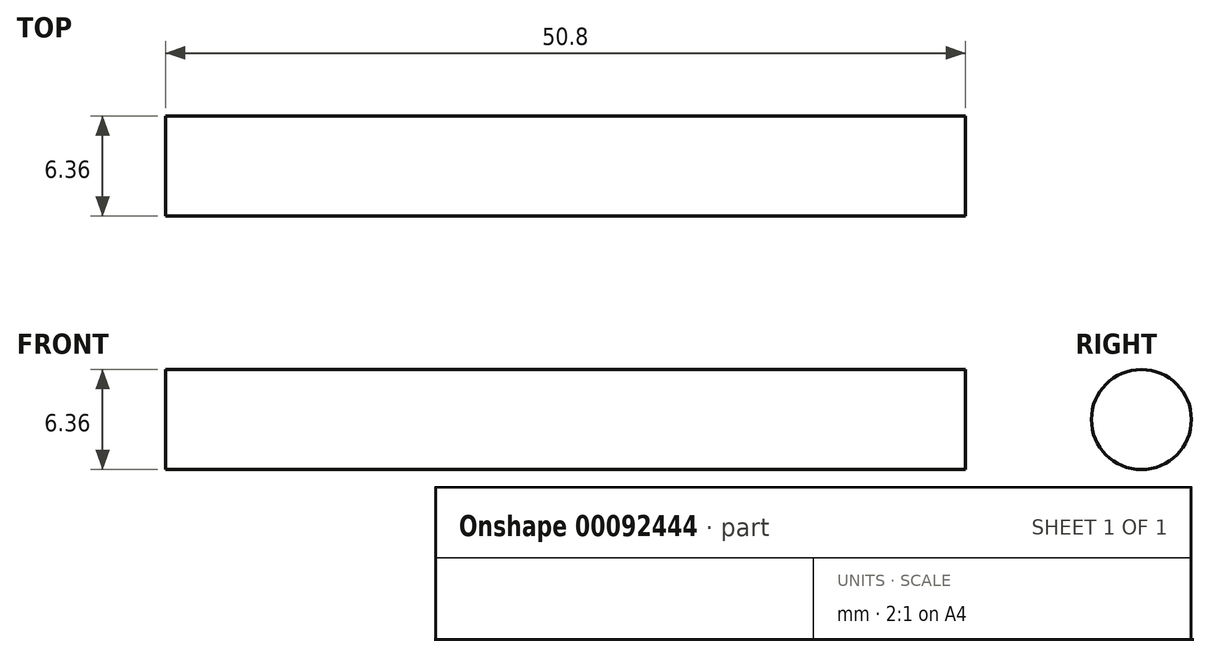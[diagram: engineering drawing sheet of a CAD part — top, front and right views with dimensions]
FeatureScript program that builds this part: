
annotation { "Feature Type Name" : "Feature", "Feature Type Description" : "" }
export const myFeature = defineFeature(function(context is Context, id is Id, definition is map)
    precondition{}
    {
        {
            var Q0;
            Q0=qCreatedBy(makeId("Right.planeOp"),FACE);
            var sketch = newSketch(context, id + "F0", { "sketchPlane" : qUnion([Q0])});
            skCircle(sketch, "E0", {"center": v(0, 0) * mm, "radius": 3.18 * mm});
            skSolve(sketch);
        }
        {
            var Q0;
            Q0=makeQuery(id+"F0.imprint","IMPRINT",FACE,{"disambiguationData":[TD([[makeQuery(id+"F0.imprint","IMPRINT",EDGE,{"derivedFrom":sQuery(id+"F0.wireOp",EDGE,"E0")}),1.0]])]});
            extrude(context, id + "F1", {"entities" : qUnion([Q0]), "depth" : 50.8 * mm});
        }
    });
